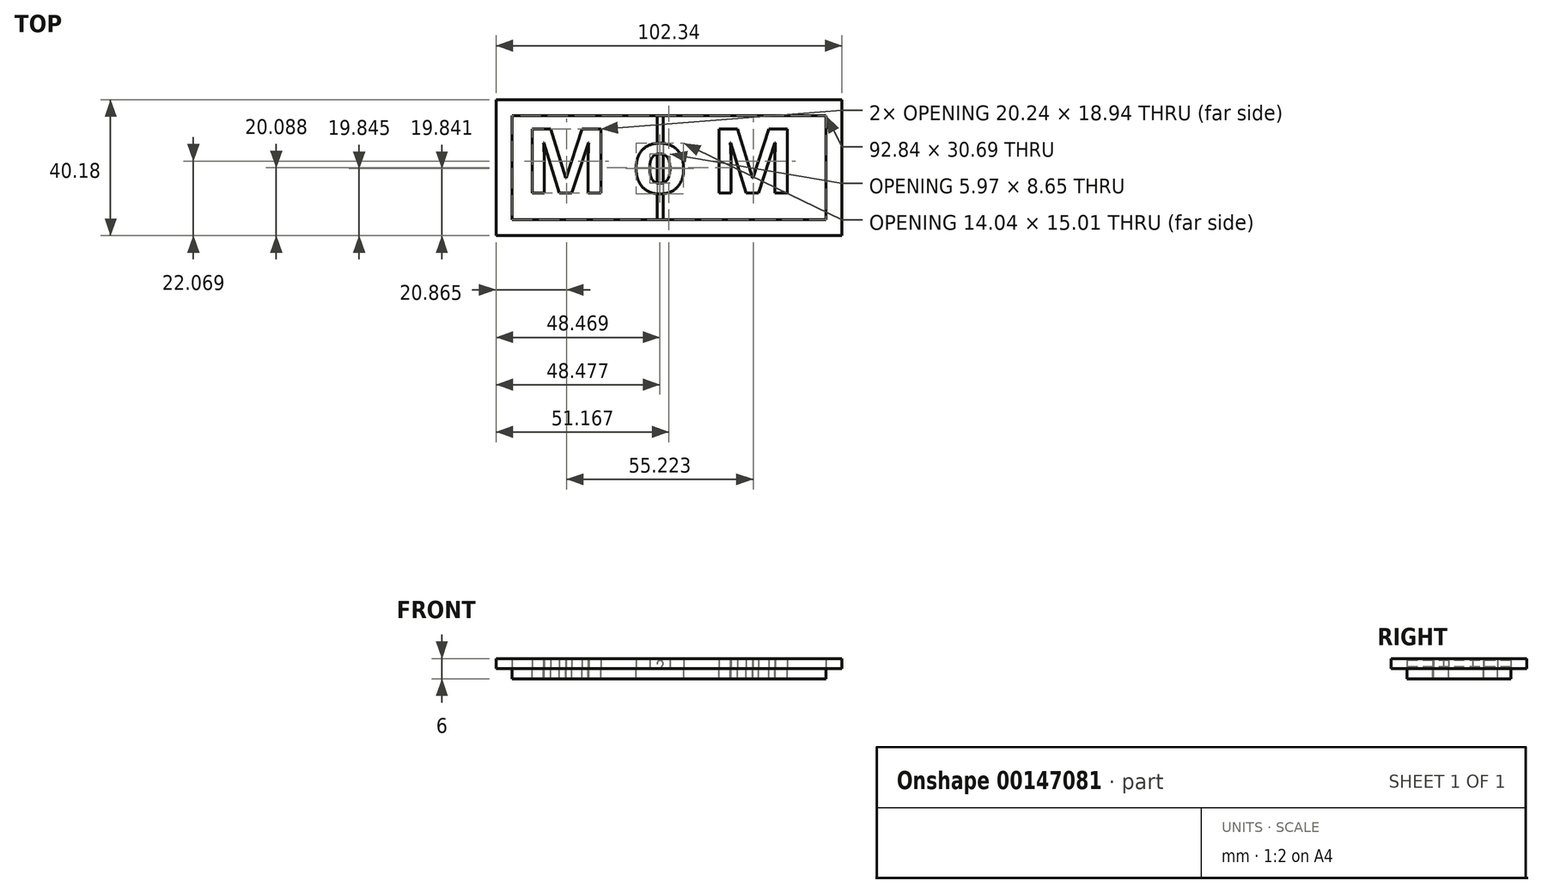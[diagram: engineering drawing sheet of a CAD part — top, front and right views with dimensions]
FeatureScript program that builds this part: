
annotation { "Feature Type Name" : "Feature", "Feature Type Description" : "" }
export const myFeature = defineFeature(function(context is Context, id is Id, definition is map)
    precondition{}
    {
        {
            var Q0;
            Q0=qCreatedBy(makeId("Top.planeOp"),FACE);
            var sketch = newSketch(context, id + "F0", { "sketchPlane" : qUnion([Q0])});
            skText(sketch, "E0", { "text": "M o M ", "fontName": "OpenSans-Bold.ttf"});
            skLineSegment(sketch, "E1.bottom", {"start": v(-8.36, 27.58) * mm, "end": v(93.98, 27.58) * mm});
            skLineSegment(sketch, "E1.top", {"start": v(-8.36, -12.6) * mm, "end": v(93.98, -12.6) * mm});
            skLineSegment(sketch, "E1.left", {"start": v(-8.36, 27.58) * mm, "end": v(-8.36, -12.6) * mm});
            skLineSegment(sketch, "E1.right", {"start": v(93.98, 27.58) * mm, "end": v(93.98, -12.6) * mm});
            skLineSegment(sketch, "E2.0", {"start": v(-3.61, 22.83) * mm, "end": v(89.23, 22.83) * mm});
            skLineSegment(sketch, "E2.1", {"start": v(-3.61, 22.83) * mm, "end": v(-3.61, -7.85) * mm});
            skLineSegment(sketch, "E2.2", {"start": v(-3.61, -7.85) * mm, "end": v(89.23, -7.85) * mm});
            skLineSegment(sketch, "E2.3", {"start": v(89.23, 22.83) * mm, "end": v(89.23, -7.85) * mm});
            const initialGuessF0  = {"E0": [0, 0, 1, 0, 0.0191]};
            skSetInitialGuess(sketch, initialGuessF0);
            skSolve(sketch);
        }
        {
            var Q0;
            Q0=makeQuery(id+"F0.imprint","IMPRINT",FACE,{"disambiguationData":[TD([[makeQuery(id+"F0.imprint","IMPRINT",EDGE,{"derivedFrom":sQuery(id+"F0.wireOp",EDGE,"E0.sketch_text.stroke-0")}),-1.0]])]});
            var Q1;
            Q1=makeQuery(id+"F0.imprint","IMPRINT",FACE,{"disambiguationData":[TD([[makeQuery(id+"F0.imprint","IMPRINT",EDGE,{"derivedFrom":sQuery(id+"F0.wireOp",EDGE,"E0.sketch_text.stroke-19")}),-1.0]])]});
            var Q2;
            Q2=makeQuery(id+"F0.imprint","IMPRINT",FACE,{"disambiguationData":[TD([[makeQuery(id+"F0.imprint","IMPRINT",EDGE,{"derivedFrom":sQuery(id+"F0.wireOp",EDGE,"E0.sketch_text.stroke-37")}),-1.0]])]});
            var Q3;
            Q3=makeQuery(id+"F0.imprint","IMPRINT",FACE,{"disambiguationData":[TD([[makeQuery(id+"F0.imprint","IMPRINT",EDGE,{"derivedFrom":sQuery(id+"F0.wireOp",EDGE,"E1.bottom")}),-1.0]])]});
            extrude(context, id + "F1", {"entities" : qUnion([Q0, Q1, Q2, Q3]), "depth" : 3 * mm});
        }
        {
            var Q0;
            Q0=makeQuery(id+"F0.imprint","IMPRINT",FACE,{"disambiguationData":[TD([[makeQuery(id+"F0.imprint","IMPRINT",EDGE,{"derivedFrom":sQuery(id+"F0.wireOp",EDGE,"E0.sketch_text.stroke-0")}),1.0]])]});
            extrude(context, id + "F2", {"entities" : qUnion([Q0]), "oppositeDirection" : true, "depth" : 3 * mm});
        }
        {
            var Q0;
            Q0=makeQuery(id+"F1.opExtrude","SWEPT_FACE",FACE,{"disambiguationData":[OSD([sQuery(id+"F0.wireOp",EDGE,"E2.2")])]});
            var sketch = newSketch(context, id + "F3", { "sketchPlane" : qUnion([Q0])});
            skCircle(sketch, "E3", {"center": v(-40.2, 1.5) * mm, "radius": 0.91 * mm});
            skSolve(sketch);
        }
        {
            var Q0;
            Q0 = qSketchRegion(id + "F3", true);
            var Q1;
            Q1=makeQuery(id+"F1.opExtrude","SWEPT_FACE",FACE,{"disambiguationData":[OSD([sQuery(id+"F0.wireOp",EDGE,"E2.0")])]});
            extrude(context, id + "F4", {"entities" : qUnion([Q0]), "endBound" : BoundingType.UP_TO_SURFACE, "endBoundEntityFace" : qUnion([Q1]), "depth" : 25 * mm});
        }
    });
